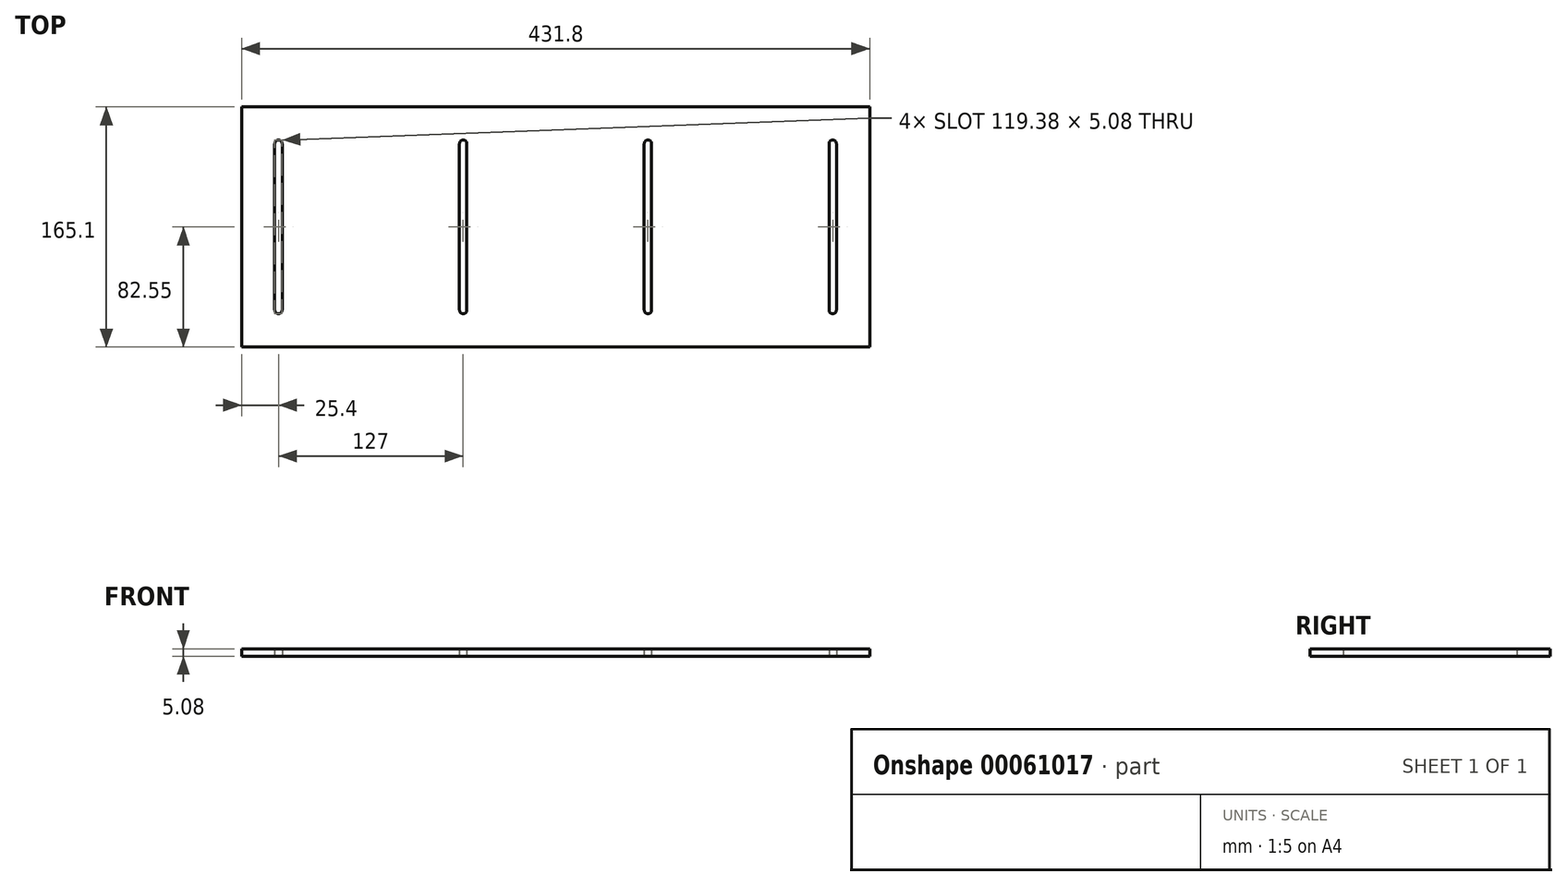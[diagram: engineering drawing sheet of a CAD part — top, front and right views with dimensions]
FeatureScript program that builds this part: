
annotation { "Feature Type Name" : "Feature", "Feature Type Description" : "" }
export const myFeature = defineFeature(function(context is Context, id is Id, definition is map)
    precondition{}
    {
        {
            var Q0;
            Q0=qCreatedBy(makeId("Top.planeOp"),FACE);
            var sketch = newSketch(context, id + "F0", { "sketchPlane" : qUnion([Q0])});
            skLineSegment(sketch, "E0.bottom", {"start": v(0, 0) * mm, "end": v(431.8, 0) * mm});
            skLineSegment(sketch, "E0.top", {"start": v(0, 165.1) * mm, "end": v(431.8, 165.1) * mm});
            skLineSegment(sketch, "E0.left", {"start": v(0, 0) * mm, "end": v(0, 165.1) * mm});
            skLineSegment(sketch, "E0.right", {"start": v(431.8, 0) * mm, "end": v(431.8, 165.1) * mm});
            skLineSegment(sketch, "E1.left", {"start": v(22.86, 139.7) * mm, "end": v(22.86, 25.4) * mm});
            skLineSegment(sketch, "E1.right", {"start": v(27.94, 139.7) * mm, "end": v(27.94, 25.4) * mm});
            skArc(sketch, "E2", {"start": v(22.86, 139.7) * mm, "mid": v(25.4, 142.24) * mm, "end": v(27.94, 139.7) * mm});
            skArc(sketch, "E3", {"start": v(27.94, 25.4) * mm, "mid": v(25.4, 22.86) * mm, "end": v(22.86, 25.4) * mm});
            skLineSegment(sketch, "E4.1.0.0", {"start": v(154.94, 139.7) * mm, "end": v(154.94, 25.4) * mm});
            skLineSegment(sketch, "E4.1.0.1", {"start": v(149.86, 139.7) * mm, "end": v(149.86, 25.4) * mm});
            skArc(sketch, "E4.1.0.2", {"start": v(154.94, 25.4) * mm, "mid": v(152.4, 22.86) * mm, "end": v(149.86, 25.4) * mm});
            skArc(sketch, "E4.1.0.3", {"start": v(149.86, 139.7) * mm, "mid": v(152.4, 142.24) * mm, "end": v(154.94, 139.7) * mm});
            skLineSegment(sketch, "E4.2.0.0", {"start": v(281.94, 139.7) * mm, "end": v(281.94, 25.4) * mm});
            skLineSegment(sketch, "E4.2.0.1", {"start": v(276.86, 139.7) * mm, "end": v(276.86, 25.4) * mm});
            skArc(sketch, "E4.2.0.2", {"start": v(281.94, 25.4) * mm, "mid": v(279.4, 22.86) * mm, "end": v(276.86, 25.4) * mm});
            skArc(sketch, "E4.2.0.3", {"start": v(276.86, 139.7) * mm, "mid": v(279.4, 142.24) * mm, "end": v(281.94, 139.7) * mm});
            skLineSegment(sketch, "E4.3.0.0", {"start": v(408.94, 139.7) * mm, "end": v(408.94, 25.4) * mm});
            skLineSegment(sketch, "E4.3.0.1", {"start": v(403.86, 139.7) * mm, "end": v(403.86, 25.4) * mm});
            skArc(sketch, "E4.3.0.2", {"start": v(408.94, 25.4) * mm, "mid": v(406.4, 22.86) * mm, "end": v(403.86, 25.4) * mm});
            skArc(sketch, "E4.3.0.3", {"start": v(403.86, 139.7) * mm, "mid": v(406.4, 142.24) * mm, "end": v(408.94, 139.7) * mm});
            skLineSegment(sketch, "E4.direction1", {"start": v(22.86, 25.4) * mm, "end": v(149.86, 25.4) * mm, "construction": true});
            skSolve(sketch);
        }
        {
            var Q0;
            Q0 = qSketchRegion(id + "F0", true);
            extrude(context, id + "F1", {"entities" : qUnion([Q0]), "depth" : 5.08 * mm});
        }
    });
